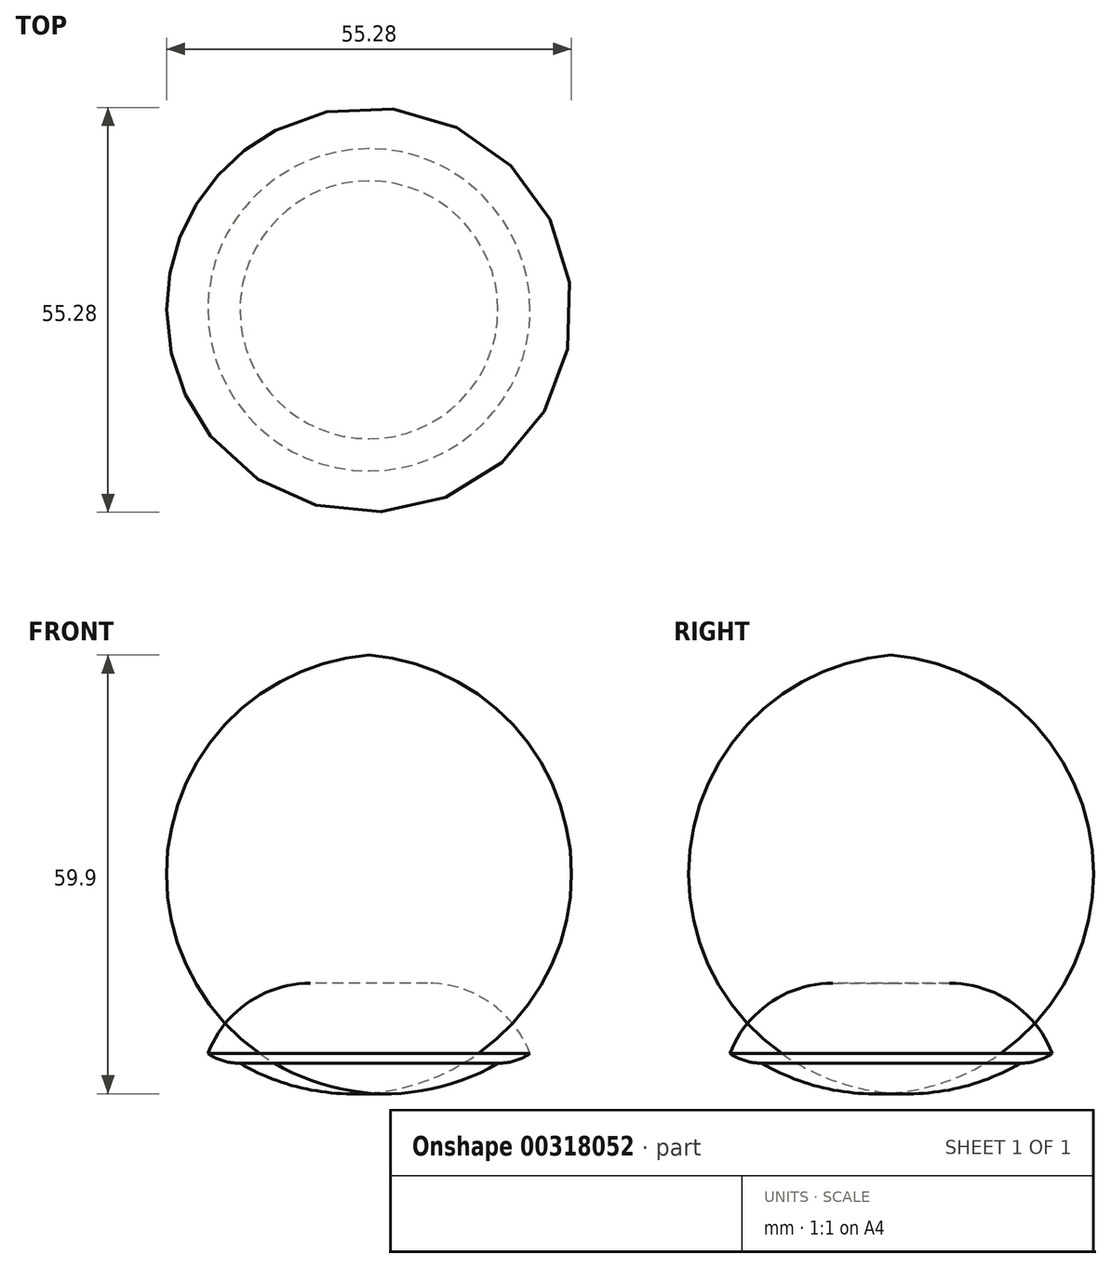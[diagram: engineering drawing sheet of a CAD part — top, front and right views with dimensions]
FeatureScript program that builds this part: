
annotation { "Feature Type Name" : "Feature", "Feature Type Description" : "" }
export const myFeature = defineFeature(function(context is Context, id is Id, definition is map)
    precondition{}
    {
        {
            var Q0;
            Q0=qCreatedBy(makeId("Front.planeOp"),FACE);
            var sketch = newSketch(context, id + "F0", { "sketchPlane" : qUnion([Q0])});
            skLineSegment(sketch, "E0", {"start": v(0, 0) * mm, "end": v(8, 0) * mm});
            skArc(sketch, "E1", {"start": v(22, -9.61) * mm, "mid": v(16.5, -2.64) * mm, "end": v(8, 0) * mm});
            skLineSegment(sketch, "E2", {"start": v(0, 0) * mm, "end": v(0, -60.19) * mm});
            skArc(sketch, "E3", {"start": v(17.6, -10.93) * mm, "mid": v(19.9, -10.6) * mm, "end": v(22, -9.61) * mm});
            skLineSegment(sketch, "E4", {"start": v(17.6, -10.93) * mm, "end": v(0, -10.93) * mm});
            skArc(sketch, "E5", {"start": v(0, -15) * mm, "mid": v(9.12, -14.32) * mm, "end": v(17.6, -10.93) * mm});
            skLineSegment(sketch, "E6", {"start": v(15.77, -11.93) * mm, "end": v(0, -11.93) * mm});
            skSolve(sketch);
        }
        {
            var Q0;
            {var subQ3=sQuery(id+"F0.wireOp",EDGE,"E6");Q0=makeQuery(id+"F0.imprint","IMPRINT",FACE,{"disambiguationData":[TD([[makeQuery(id+"F0.imprint","IMPRINT",EDGE,{"derivedFrom":subQ3}),1.0]])]});}
            var Q1;
            {var subQ0=sQuery(id+"F0.wireOp",EDGE,"E4");Q1=makeQuery(id+"F0.imprint","IMPRINT",FACE,{"disambiguationData":[TD([[makeQuery(id+"F0.imprint","IMPRINT",EDGE,{"derivedFrom":subQ0}),1.0]])]});}
            var Q2;
            {var subQ1=sQuery(id+"F0.wireOp",EDGE,"E0");Q2=makeQuery(id+"F0.imprint","IMPRINT",FACE,{"disambiguationData":[TD([[makeQuery(id+"F0.imprint","IMPRINT",EDGE,{"derivedFrom":subQ1}),-1.0]])]});}
            var Q3;
            Q3=sQuery(id+"F0.wireOp",EDGE,"E2");
            revolve(context, id + "F1", {"entities" : qUnion([Q0, Q1, Q2]), "axis" : qUnion([Q3]), "revolveType" : RevolveType.FULL});
        }
    });
